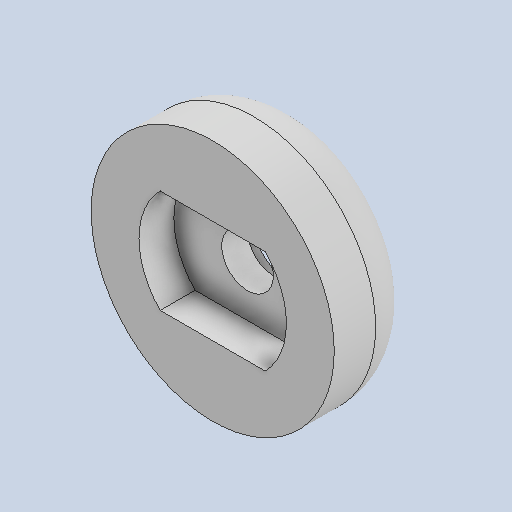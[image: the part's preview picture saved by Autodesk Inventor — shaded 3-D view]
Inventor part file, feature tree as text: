
AUTODESK INVENTOR PART (.ipt)
format: ipt  version: 2022 (Build 260153070, 153G)  size: 141,824 bytes
history: native  units: in
note: dims shown in document units (in); Inventor stores cm internally (conversion verified against a paired STEP export)
features: other x3, sketch x3, plane x1
ambient origin geometry x8: Origin, YZ Plane, XZ Plane, XY Plane, X Axis, Y Axis, Z Axis, Center Point
bodies: Solid1 (feature_tree)
feature tree (7):
  other  "TTencodercap.ipt"
  other  "Solid1::TTencodercap.ipt"
  other  "TaggingFeature1"
  sketch  "Sketch1"  dims[d0=0.3937in]
  sketch  "Sketch2"
  sketch  "Sketch3"
  plane  "Work Plane1"
